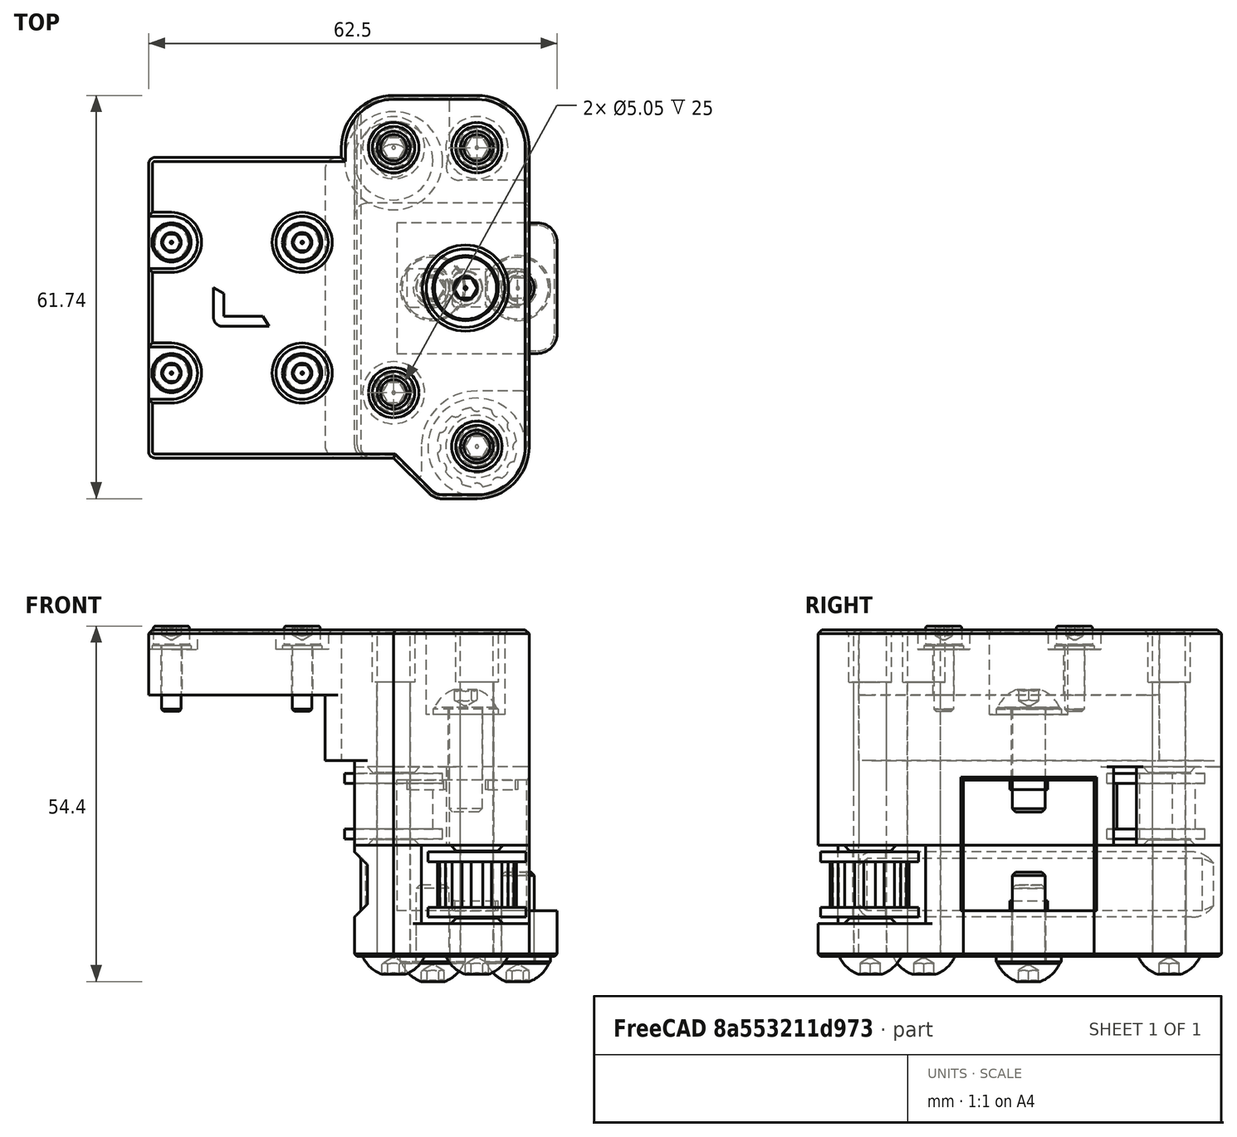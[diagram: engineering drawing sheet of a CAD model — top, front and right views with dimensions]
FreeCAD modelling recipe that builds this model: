
FCSTD DOCUMENT  (FreeCAD 0.19R24291 (Git))
Label: y-carrier-left-2020-assembly
License: Other
LicenseURL: GPL3
objects: Part::FeaturePython×18, Part::Feature×4, App::Part×1
note: 22 computed .brp shape members not serialized (recipe doc carries the construction recipe); baked Part::Feature solids carry a one-line shape summary decoded from their .brp

FEATURE [Part::Feature] Cut001002  label="smooth-idler"
  Placement = pos=(-2,0.5,0) rot=(0,0,1;0rad)
  shape: bbox 15 x 15 x 10 mm, 8 faces (baked)
FEATURE [Part::Feature] Cut002001001  label="20t-idler"
  Placement = pos=(0,-4.61,0) rot=(0,0,1;0rad)
  shape: bbox 15 x 15 x 10 mm, 31 faces (baked)
FEATURE [Part::Feature] Chamfer030006001
  Placement = pos=(0,0,3) rot=(0,0,1;0rad)
  shape: bbox 31 x 61.74 x 17.85 mm, 87 faces (baked)
FEATURE [Part::FeaturePython] Washer  label="M5-Washer"  # Fasteners workbench fastener (typed FeaturePython)
  Placement = pos=(28,0,3) rot=(-1,0,0;3.14159rad)
  baseObject = -> Chamfer030006001 [Edge94]
  diameter = 1
  invert = false
  matchOuter = false
  offset = 0
  type = 4
FEATURE [Part::FeaturePython] Screw  label="M5x14-Screw"  # Fasteners workbench fastener (typed FeaturePython)
  Placement = pos=(28,1e-16,1.9) rot=(-1,0,0;3.14159rad)
  baseObject = -> Washer [Edge1]
  diameter = 3
  invert = false
  length = 3
  lengthCustom = 14
  matchOuter = true
  offset = 0
  thread = false
  type = 39
FEATURE [Part::FeaturePython] Washer001  label="M5-Washer001"  # Fasteners workbench fastener (typed FeaturePython)
  Placement = pos=(15,0,3) rot=(-1,0,0;3.14159rad)
  baseObject = -> Chamfer030006001 [Edge96]
  diameter = 1
  invert = false
  matchOuter = true
  offset = 0
  type = 4
FEATURE [Part::FeaturePython] Screw001  label="M5x12-Screw"  # Fasteners workbench fastener (typed FeaturePython)
  Placement = pos=(15,1e-16,1.9) rot=(-1,0,0;3.14159rad)
  baseObject = -> Washer001 [Edge1]
  diameter = 3
  invert = false
  length = 2
  lengthCustom = 12
  matchOuter = true
  offset = 0
  thread = false
  type = 39
FEATURE [Part::Feature] Cut002001002
  Placement = pos=(0,0,3) rot=(0,0,1;0rad)
  shape: bbox 58.24 x 61.74 x 33.85 mm, 135 faces (baked)
FEATURE [Part::FeaturePython] Washer002  label="M5-Washer002"  # Fasteners workbench fastener (typed FeaturePython)
  Placement = pos=(20,0,40) rot=(0,0,1;0rad)
  baseObject = -> Cut002001002 [Edge208]
  diameter = 1
  invert = false
  matchOuter = true
  offset = 0
  type = 4
FEATURE [Part::FeaturePython] Screw002  label="M5x16-Screw"  # Fasteners workbench fastener (typed FeaturePython)
  Placement = pos=(20,0,41.1) rot=(0,0,1;0rad)
  baseObject = -> Washer002 [Edge1]
  diameter = 3
  invert = false
  length = 4
  lengthCustom = 16
  matchOuter = true
  offset = 0
  thread = false
  type = 39
FEATURE [Part::FeaturePython] Screw003  label="M5x50-Screw"  # Fasteners workbench fastener (typed FeaturePython)
  Placement = pos=(9,-16,3) rot=(-1,0,0;3.14159rad)
  baseObject = -> Chamfer030006001 [Edge97]
  diameter = 3
  invert = true
  length = 11
  lengthCustom = 50
  matchOuter = true
  offset = 0
  thread = false
  type = 39
FEATURE [Part::FeaturePython] Screw004  label="M5x50-Screw001"  # Fasteners workbench fastener (typed FeaturePython)
  Placement = pos=(9,21.5,3) rot=(-1,0,0;3.14159rad)
  baseObject = -> Chamfer030006001 [Edge100]
  diameter = 3
  invert = true
  length = 11
  lengthCustom = 50
  matchOuter = true
  offset = 0
  thread = false
  type = 39
FEATURE [Part::FeaturePython] Screw005  label="M5x50-Screw002"  # Fasteners workbench fastener (typed FeaturePython)
  Placement = pos=(21.74,21.5,3) rot=(-1,0,0;3.14159rad)
  baseObject = -> Chamfer030006001 [Edge98]
  diameter = 3
  invert = true
  length = 11
  lengthCustom = 50
  matchOuter = true
  offset = 0
  thread = false
  type = 39
FEATURE [Part::FeaturePython] Screw006  label="M5x50-Screw003"  # Fasteners workbench fastener (typed FeaturePython)
  Placement = pos=(21.74,-24.24,3) rot=(-1,0,0;3.14159rad)
  baseObject = -> Chamfer030006001 [Edge99]
  diameter = 3
  invert = true
  length = 11
  lengthCustom = 50
  matchOuter = true
  offset = 0
  thread = false
  type = 39
FEATURE [Part::FeaturePython] Washer003  label="M3-Washer"  # Fasteners workbench fastener (typed FeaturePython)
  Placement = pos=(-25,-13,50) rot=(0,0,1;0rad)
  baseObject = -> Cut002001002 [Edge298]
  diameter = 4
  invert = false
  matchOuter = true
  offset = 0
  type = 5
FEATURE [Part::FeaturePython] Washer004  label="M3-Washer001"  # Fasteners workbench fastener (typed FeaturePython)
  Placement = pos=(-25,7,50) rot=(0,0,1;0rad)
  baseObject = -> Cut002001002 [Edge302]
  diameter = 4
  invert = false
  matchOuter = true
  offset = 0
  type = 5
FEATURE [Part::FeaturePython] Washer005  label="M3-Washer002"  # Fasteners workbench fastener (typed FeaturePython)
  Placement = pos=(-5,7,50) rot=(0,0,1;0rad)
  baseObject = -> Cut002001002 [Edge300]
  diameter = 4
  invert = false
  matchOuter = true
  offset = 0
  type = 5
FEATURE [Part::FeaturePython] Washer006  label="M3-Washer003"  # Fasteners workbench fastener (typed FeaturePython)
  Placement = pos=(-5,-13,50) rot=(0,0,1;0rad)
  baseObject = -> Cut002001002 [Edge296]
  diameter = 4
  invert = false
  matchOuter = true
  offset = 0
  type = 5
FEATURE [Part::FeaturePython] Screw007  label="M3x10-Screw"  # Fasteners workbench fastener (typed FeaturePython)
  Placement = pos=(-25,7,50.55) rot=(0,0,1;0rad)
  baseObject = -> Washer004 [Edge1]
  diameter = 4
  invert = false
  length = 3
  lengthCustom = 10
  matchOuter = true
  offset = 0
  thread = false
  type = 33
FEATURE [Part::FeaturePython] Screw008  label="M3x10-Screw001"  # Fasteners workbench fastener (typed FeaturePython)
  Placement = pos=(-25,-13,50.55) rot=(0,0,1;0rad)
  baseObject = -> Washer003 [Edge1]
  diameter = 4
  invert = false
  length = 3
  lengthCustom = 10
  matchOuter = true
  offset = 0
  thread = false
  type = 33
FEATURE [Part::FeaturePython] Screw009  label="M3x10-Screw002"  # Fasteners workbench fastener (typed FeaturePython)
  Placement = pos=(-5,-13,50.55) rot=(0,0,1;0rad)
  baseObject = -> Washer006 [Edge1]
  diameter = 4
  invert = false
  length = 3
  lengthCustom = 10
  matchOuter = true
  offset = 0
  thread = false
  type = 33
FEATURE [Part::FeaturePython] Screw010  label="M3x10-Screw003"  # Fasteners workbench fastener (typed FeaturePython)
  Placement = pos=(-5,7,50.55) rot=(0,0,1;0rad)
  baseObject = -> Washer005 [Edge1]
  diameter = 4
  invert = false
  length = 3
  lengthCustom = 10
  matchOuter = true
  offset = 0
  thread = false
  type = 33
FEATURE [App::Part] Part  label="Y-carrier-left"
  Group = -> [Cut001002,Cut002001001,Chamfer030006001,Screw,Washer001,Screw001,Washer,Cut002001002,Washer003,Washer004,Washer005,Screw002,Screw007,Washer006,Screw009,Screw008,Screw010,Washer002,Screw006,Screw004,Screw005,Screw003]
  Origin = -> Origin
